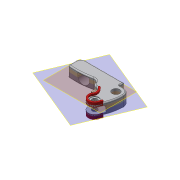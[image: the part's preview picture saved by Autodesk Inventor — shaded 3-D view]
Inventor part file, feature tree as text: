
AUTODESK INVENTOR PART (.ipt)
format: ipt  version: 2016 (Build 200138000, 138)  size: 711,168 bytes
history: native  units: in
note: dims shown in document units (in); Inventor stores cm internally (conversion verified against a paired STEP export)
features: plane x2, other x1, extrude x1, fillet x1, mirror x1, imported_body x1, sketch x1, projected_geometry x1
ambient origin geometry x8: Origin, YZ Plane, XZ Plane, XY Plane, X Axis, Y Axis, Z Axis, Center Point
bodies: Solid1 (feature_tree), Solid2 (feature_tree)
feature tree (9):
  other  "033-fe_lever-0425_stp.ipt1"
  plane  "Work Plane1"
  extrude  "Extrusion1"  Depth=0.0217in
  fillet  "Fillet1"  Radius=0.1378in
  plane  "Work Plane2"
  mirror  "Mirror1"
  imported_body  "Base1"
  sketch  "Sketch1"  dims[d0=-0.0787in d1=0.0512in d2=0.1378in d3=0.0in d4=0.0217in]
  projected_geometry  "Project Cut Edges1"
